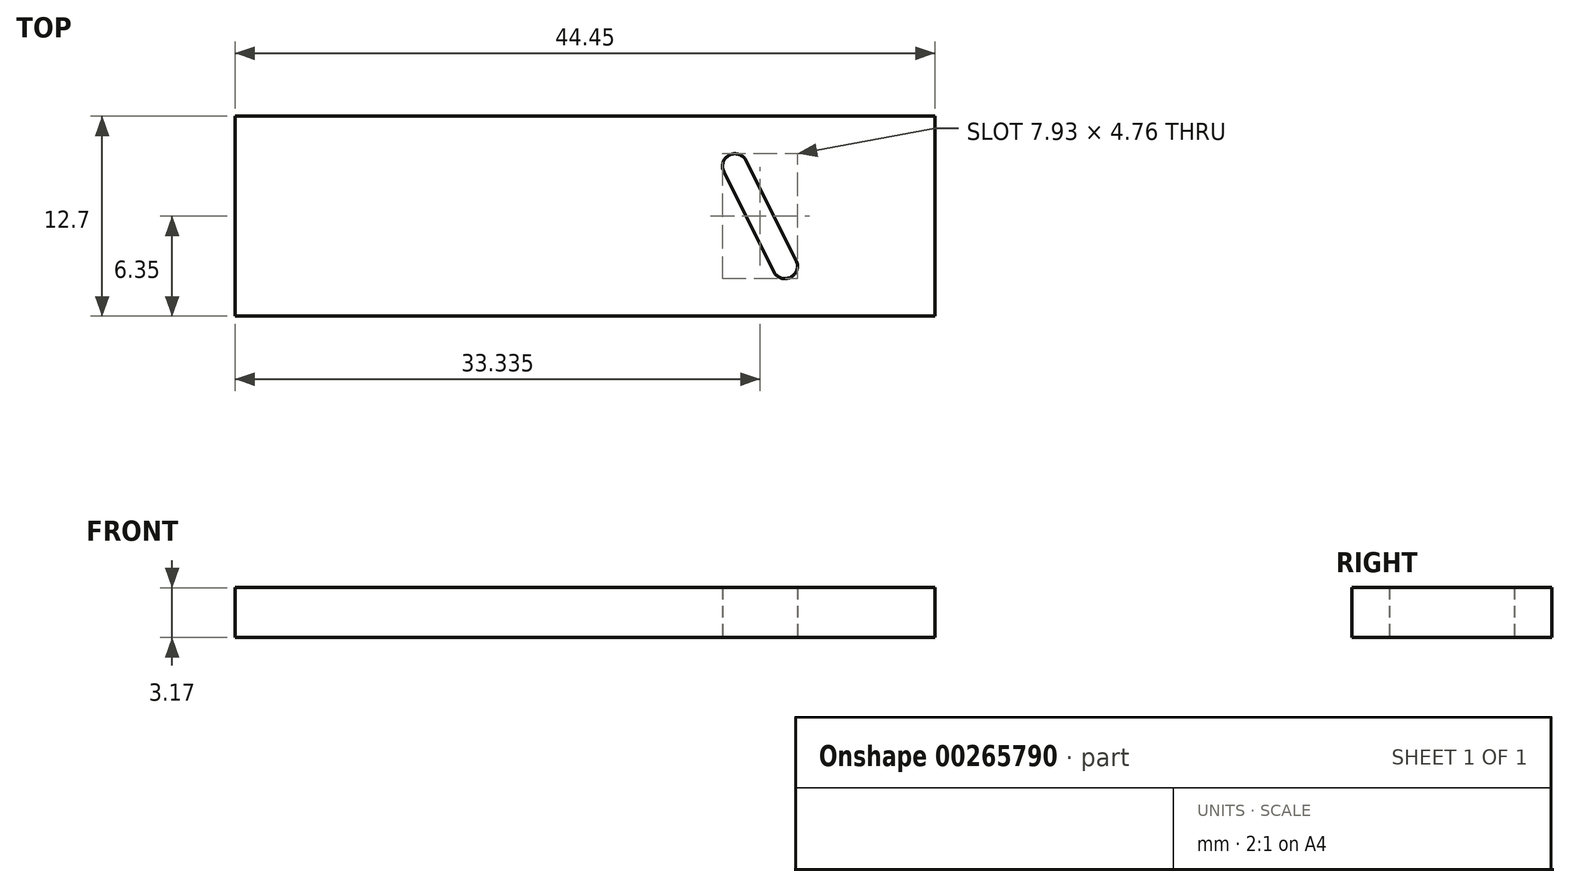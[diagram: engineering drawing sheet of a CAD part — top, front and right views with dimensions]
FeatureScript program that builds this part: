
annotation { "Feature Type Name" : "Feature", "Feature Type Description" : "" }
export const myFeature = defineFeature(function(context is Context, id is Id, definition is map)
    precondition{}
    {
        {
            var Q0;
            Q0=qCreatedBy(makeId("Top.planeOp"),FACE);
            var sketch = newSketch(context, id + "F0", { "sketchPlane" : qUnion([Q0])});
            skLineSegment(sketch, "E0.bottom", {"start": v(20.64, -6.35) * mm, "end": v(-23.81, -6.35) * mm});
            skLineSegment(sketch, "E0.top", {"start": v(20.64, 6.35) * mm, "end": v(-23.81, 6.35) * mm});
            skLineSegment(sketch, "E0.left", {"start": v(20.64, -6.35) * mm, "end": v(20.64, 6.35) * mm});
            skLineSegment(sketch, "E0.right", {"start": v(-23.81, -6.35) * mm, "end": v(-23.81, 6.35) * mm});
            skPoint(sketch, "E0.middle", {"position": v(115.89, 0) * mm});
            skSolve(sketch);
        }
        {
            var Q0;
            Q0 = qSketchRegion(id + "F0", true);
            extrude(context, id + "F1", {"entities" : qUnion([Q0]), "depth" : 3.17 * mm});
        }
        {
            var Q0;
            Q0=qCreatedBy(makeId("Top.planeOp"),FACE);
            var sketch = newSketch(context, id + "F2", { "sketchPlane" : qUnion([Q0])});
            skLineSegment(sketch, "E1", {"start": v(7.94, 3.17) * mm, "end": v(11.11, -3.18) * mm});
            skArc(sketch, "E2.0.startCap", {"start": v(7.23, 2.82) * mm, "mid": v(7.58, 3.88) * mm, "end": v(8.65, 3.53) * mm});
            skArc(sketch, "E2.0.endCap", {"start": v(11.82, -2.82) * mm, "mid": v(11.47, -3.88) * mm, "end": v(10.4, -3.53) * mm});
            skLineSegment(sketch, "E2.0.left", {"start": v(8.65, 3.53) * mm, "end": v(11.82, -2.82) * mm});
            skLineSegment(sketch, "E2.0.right", {"start": v(7.23, 2.82) * mm, "end": v(10.4, -3.53) * mm});
            skSolve(sketch);
        }
        {
            var Q0;
            Q0 = qSketchRegion(id + "F2", true);
            extrude(context, id + "F3", {"entities" : qUnion([Q0]), "operationType" : NewBodyOperationType.REMOVE, "endBound" : BoundingType.THROUGH_ALL, "depth" : 25.4 * mm});
        }
    });
